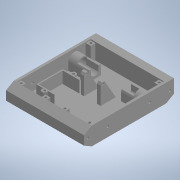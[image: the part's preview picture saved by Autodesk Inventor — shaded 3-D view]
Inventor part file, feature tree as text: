
AUTODESK INVENTOR PART (.ipt)
format: ipt  version: 2020 (Build 240168000, 168)  size: 487,424 bytes
history: native  units: in
note: dims shown in document units (in); Inventor stores cm internally (conversion verified against a paired STEP export)
features: extrude x15, sketch x15, projected_geometry x15, mirror x4, plane x1
ambient origin geometry x8: Origin, YZ Plane, XZ Plane, XY Plane, X Axis, Y Axis, Z Axis, Center Point
bodies: Solid1 (feature_tree)
feature tree (50):
  extrude  "Extrusion1"  Depth=5.9055in
  extrude  "Extrusion2"  TaperAngle=0.0deg  [1 undecoded]
  extrude  "Extrusion3"  Depth=1.063in
  extrude  "Extrusion4"  Depth=0.315in
  extrude  "Extrusion5"  TaperAngle=0.0deg  [1 undecoded]
  extrude  "Extrusion6"  Depth=0.5906in
  mirror  "Mirror1"
  extrude  "Extrusion7"  Depth=0.0787in
  mirror  "Mirror2"
  extrude  "Extrusion8"  Depth=0.6102in
  mirror  "Mirror3"
  plane  "Work Plane1"
  extrude  "Extrusion9"  Depth=0.7874in TaperAngle=0.0deg
  mirror  "Mirror4"
  extrude  "Extrusion10"  Depth=6.063in TaperAngle=0.0deg
  extrude  "Extrusion11"  Depth=0.1575in
  extrude  "Extrusion12"  TaperAngle=0.0deg  [1 undecoded]
  extrude  "Extrusion13"  Depth=0.2756in
  extrude  "Extrusion14"  Depth=0.4331in
  extrude  "Extrusion15"  Depth=2.7559in
  sketch  "Sketch1"  dims[d0=1.1811in d1=5.9055in]
  sketch  "Sketch2"  dims[d2=5.1181in d3=0.0in]
  projected_geometry  "Projected Loop1"
  sketch  "Sketch3"  dims[d4=0.1575in d5=1.063in]
  projected_geometry  "Projected Loop2"
  projected_geometry  "Projected Loop3"
  sketch  "Sketch4"  dims[d6=0.0in d8=0.315in]
  sketch  "Sketch5"  dims[d10=0.993in d11=0.0in]
  projected_geometry  "Projected Loop4"
  sketch  "Sketch6"  dims[d12=0.6496in d13=0.5906in]
  sketch  "Sketch7"  dims[d14=1.5748in d15=0.0787in]
  sketch  "Sketch9"  dims[d16=0.5512in d17=0.0in d18=0.6102in]
  sketch  "Sketch10"  dims[d19=0.4803in d20=0.7874in d21=0.0in]
  sketch  "Sketch12"  dims[d22=0.1654in d23=6.063in d24=0.0in]
  projected_geometry  "Projected Loop6"
  projected_geometry  "Projected Loop7"
  projected_geometry  "Projected Loop8"
  sketch  "Sketch13"  dims[d25=0.5114in d26=0.1575in]
  projected_geometry  "Projected Loop9"
  projected_geometry  "Projected Loop10"
  projected_geometry  "Projected Loop11"
  projected_geometry  "Projected Loop12"
  projected_geometry  "Projected Loop13"
  projected_geometry  "Projected Loop14"
  sketch  "Sketch14"  dims[d27=1.5748in d28=0.0in d29=0.0in]
  sketch  "Sketch15"  dims[d30=0.1575in d31=0.2756in]
  projected_geometry  "Projected Loop15"
  sketch  "Sketch16"  dims[d32=0.0in d33=0.4331in]
  sketch  "Sketch17"  dims[d34=0.122in d38=2.7559in d40=0.061in d41=0.0909in d42=0.2362in d43=0.0in d44=60.0deg d45=0.0787in d46=0.315in d48=0.993in d49=0.0in d51=0.1575in d52=0.1575in d53=0.2756in d54=0.0in d55=0.4724in d56=1.1614in d57=1.5748in d58=1.5945in d59=0.0787in d60=0.0787in d62=0.315in d63=0.7677in d64=0.0in d65=0.1575in d66=0.1575in d67=0.2756in d68=0.0in d69=0.8268in d70=0.2953in d71=0.0394in d72=0.0in d73=0.7677in d74=0.0in]
  projected_geometry  "Projected Loop16"
note: 3 required parameter values undecoded (feature->parameter linkage not recoverable at this tier; creation-order binding heuristic only, values carry confidence <= 0.55)
